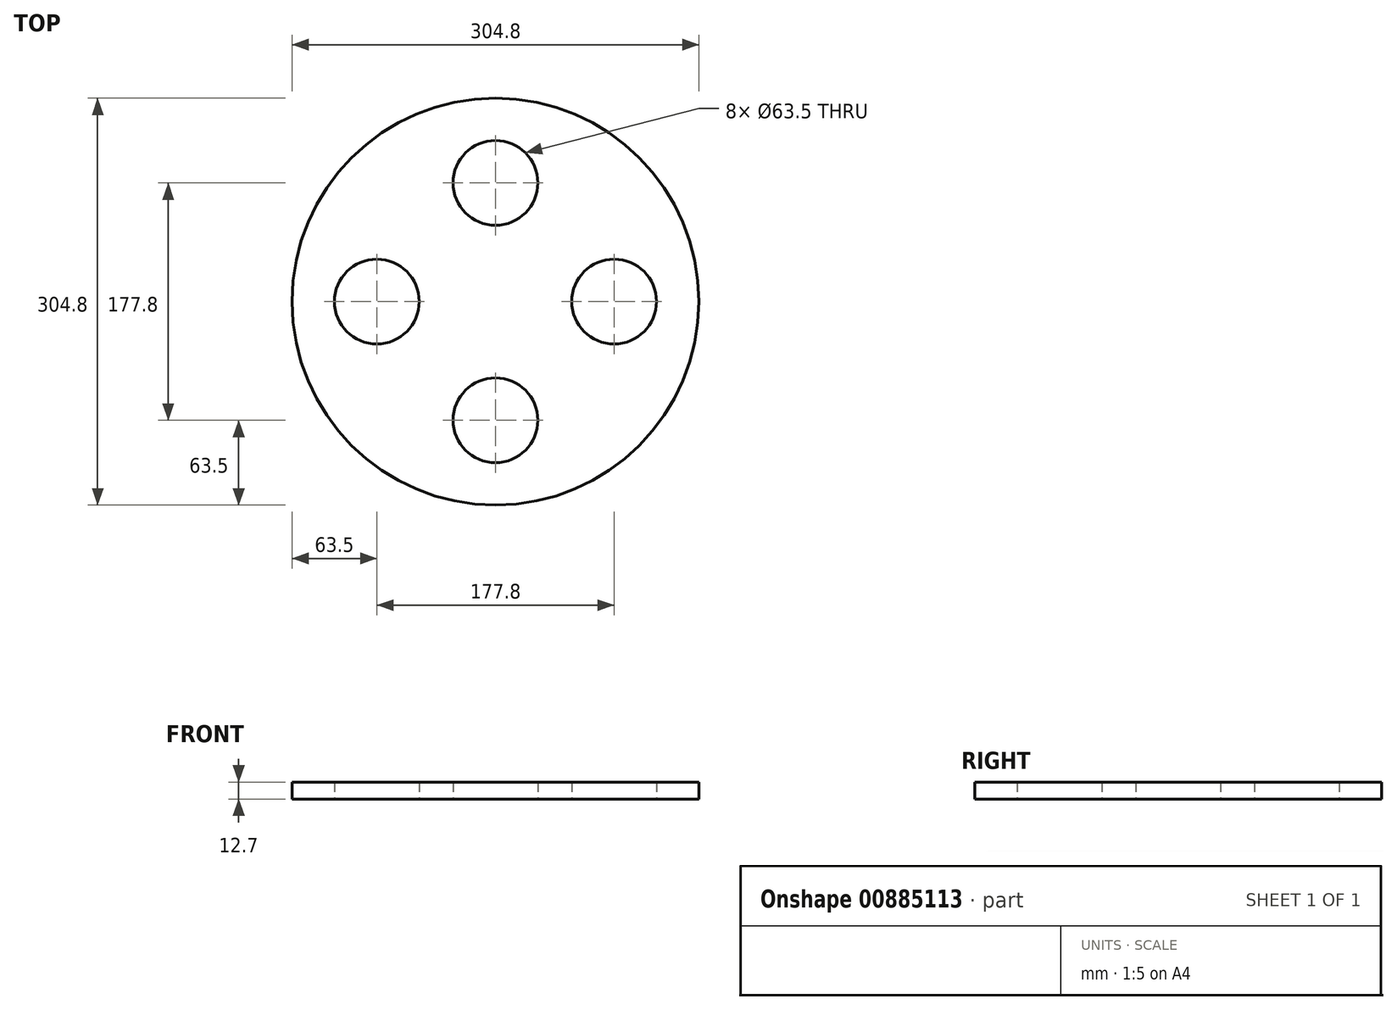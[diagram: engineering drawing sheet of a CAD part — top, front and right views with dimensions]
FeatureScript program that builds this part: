
annotation { "Feature Type Name" : "Feature", "Feature Type Description" : "" }
export const myFeature = defineFeature(function(context is Context, id is Id, definition is map)
    precondition{}
    {
        {
            var Q0;
            Q0=qCreatedBy(makeId("Top.planeOp"),FACE);
            var sketch = newSketch(context, id + "F0", { "sketchPlane" : qUnion([Q0])});
            skCircle(sketch, "E0", {"center": v(0, 0) * mm, "radius": 152.4 * mm});
            skCircle(sketch, "E1", {"center": v(0, 0) * mm, "radius": 139.7 * mm, "construction": true});
            skCircle(sketch, "E2", {"center": v(0, 88.9) * mm, "radius": 50.8 * mm, "construction": true});
            skLineSegment(sketch, "E3", {"start": v(0, 88.9) * mm, "end": v(0, 0) * mm, "construction": true});
            skCircle(sketch, "E4", {"center": v(0, 88.9) * mm, "radius": 31.75 * mm});
            skCircle(sketch, "E5.1.0", {"center": v(-88.9, 0) * mm, "radius": 31.75 * mm});
            skCircle(sketch, "E5.1.1", {"center": v(-88.9, 0) * mm, "radius": 50.8 * mm, "construction": true});
            skCircle(sketch, "E5.2.0", {"center": v(0, -88.9) * mm, "radius": 31.75 * mm});
            skCircle(sketch, "E5.2.1", {"center": v(0, -88.9) * mm, "radius": 50.8 * mm, "construction": true});
            skCircle(sketch, "E5.3.0", {"center": v(88.9, 0) * mm, "radius": 31.75 * mm});
            skCircle(sketch, "E5.3.1", {"center": v(88.9, 0) * mm, "radius": 50.8 * mm, "construction": true});
            skSolve(sketch);
        }
        {
            var Q0;
            Q0=makeQuery(id+"F0.imprint","IMPRINT",FACE,{"disambiguationData":[TD([[makeQuery(id+"F0.imprint","IMPRINT",EDGE,{"derivedFrom":sQuery(id+"F0.wireOp",EDGE,"E0")}),1.0]])]});
            extrude(context, id + "F1", {"entities" : qUnion([Q0]), "depth" : 12.7 * mm, "offsetDistance" : 25.4 * mm});
        }
    });
